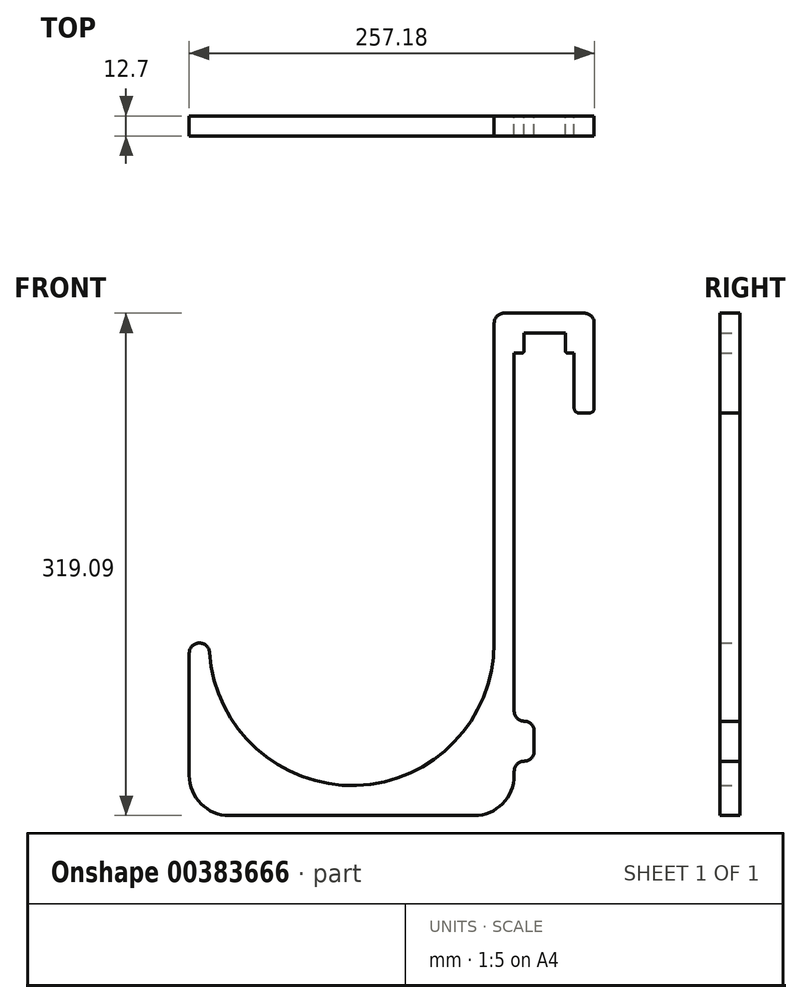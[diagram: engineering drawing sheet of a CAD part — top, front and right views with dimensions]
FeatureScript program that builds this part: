
annotation { "Feature Type Name" : "Feature", "Feature Type Description" : "" }
export const myFeature = defineFeature(function(context is Context, id is Id, definition is map)
    precondition{}
    {
        {
            var Q0;
            Q0=qCreatedBy(makeId("Front.planeOp"),FACE);
            var sketch = newSketch(context, id + "F0", { "sketchPlane" : qUnion([Q0])});
            skArc(sketch, "E0", {"start": v(-90.3, -5.93) * mm, "mid": v(2.97, -90.44) * mm, "end": v(90.49, 0) * mm});
            skLineSegment(sketch, "E1", {"start": v(90.49, 0) * mm, "end": v(90.49, 203.2) * mm});
            skLineSegment(sketch, "E2", {"start": v(96.84, 209.55) * mm, "end": v(147.64, 209.55) * mm});
            skLineSegment(sketch, "E3", {"start": v(153.99, 203.2) * mm, "end": v(153.99, 149.23) * mm});
            skLineSegment(sketch, "E4", {"start": v(150.81, 146.05) * mm, "end": v(144.46, 146.05) * mm});
            skLineSegment(sketch, "E5", {"start": v(141.29, 149.23) * mm, "end": v(141.29, 184.15) * mm});
            skLineSegment(sketch, "E6", {"start": v(103.19, 184.15) * mm, "end": v(103.19, -43.3) * mm});
            skLineSegment(sketch, "E7", {"start": v(109.54, -49.65) * mm, "end": v(109.54, -49.65) * mm});
            skLineSegment(sketch, "E8", {"start": v(115.89, -56) * mm, "end": v(115.89, -68.7) * mm});
            skLineSegment(sketch, "E9", {"start": v(109.54, -75.05) * mm, "end": v(109.54, -75.05) * mm});
            skLineSegment(sketch, "E10", {"start": v(103.19, -81.4) * mm, "end": v(103.19, -84.14) * mm});
            skLineSegment(sketch, "E11", {"start": v(77.79, -109.54) * mm, "end": v(-77.79, -109.54) * mm});
            skLineSegment(sketch, "E12", {"start": v(-103.19, -84.14) * mm, "end": v(-103.19, -6.35) * mm});
            skLineSegment(sketch, "E13", {"start": v(-96.84, 0) * mm, "end": v(-96.63, 0) * mm});
            skPoint(sketch, "E14.visualSharp", {"position": v(90.49, 209.55) * mm});
            skArc(sketch, "E14.filletArc", {"start": v(96.84, 209.55) * mm, "mid": v(92.35, 207.7) * mm, "end": v(90.49, 203.2) * mm});
            skPoint(sketch, "E15.visualSharp", {"position": v(153.99, 209.55) * mm});
            skArc(sketch, "E15.filletArc", {"start": v(153.99, 203.2) * mm, "mid": v(152.13, 207.7) * mm, "end": v(147.64, 209.55) * mm});
            skPoint(sketch, "E16.visualSharp", {"position": v(141.29, 146.05) * mm});
            skArc(sketch, "E16.filletArc", {"start": v(141.29, 149.23) * mm, "mid": v(142.22, 146.98) * mm, "end": v(144.46, 146.05) * mm});
            skPoint(sketch, "E17.visualSharp", {"position": v(153.99, 146.05) * mm});
            skArc(sketch, "E17.filletArc", {"start": v(150.81, 146.05) * mm, "mid": v(153.06, 146.98) * mm, "end": v(153.99, 149.23) * mm});
            skPoint(sketch, "E18.visualSharp", {"position": v(115.89, -49.65) * mm});
            skArc(sketch, "E18.filletArc", {"start": v(115.89, -56) * mm, "mid": v(114.03, -51.5) * mm, "end": v(109.54, -49.65) * mm});
            skPoint(sketch, "E19.visualSharp", {"position": v(115.89, -75.05) * mm});
            skArc(sketch, "E19.filletArc", {"start": v(109.54, -75.05) * mm, "mid": v(114.03, -73.19) * mm, "end": v(115.89, -68.7) * mm});
            skPoint(sketch, "E20.visualSharp", {"position": v(-90.49, 0) * mm});
            skArc(sketch, "E20.filletArc", {"start": v(-90.3, -5.93) * mm, "mid": v(-92.29, -1.71) * mm, "end": v(-96.63, 0) * mm});
            skPoint(sketch, "E21.visualSharp", {"position": v(-103.19, 0) * mm});
            skArc(sketch, "E21.filletArc", {"start": v(-96.84, 0) * mm, "mid": v(-101.33, -1.86) * mm, "end": v(-103.19, -6.35) * mm});
            skPoint(sketch, "E22.visualSharp", {"position": v(-103.19, -109.54) * mm});
            skArc(sketch, "E22.filletArc", {"start": v(-103.19, -84.14) * mm, "mid": v(-95.75, -102.1) * mm, "end": v(-77.79, -109.54) * mm});
            skPoint(sketch, "E23.visualSharp", {"position": v(103.19, -109.54) * mm});
            skArc(sketch, "E23.filletArc", {"start": v(77.79, -109.54) * mm, "mid": v(95.75, -102.1) * mm, "end": v(103.19, -84.14) * mm});
            skLineSegment(sketch, "E24", {"start": v(103.19, 184.15) * mm, "end": v(108.01, 184.15) * mm});
            skLineSegment(sketch, "E25", {"start": v(109.54, 185.67) * mm, "end": v(109.54, 196.85) * mm});
            skLineSegment(sketch, "E26", {"start": v(109.54, 196.85) * mm, "end": v(135.7, 196.85) * mm});
            skLineSegment(sketch, "E27", {"start": v(135.7, 196.85) * mm, "end": v(135.7, 185.67) * mm});
            skLineSegment(sketch, "E28", {"start": v(137.22, 184.15) * mm, "end": v(141.29, 184.15) * mm});
            skPoint(sketch, "E29.visualSharp", {"position": v(109.54, 184.15) * mm});
            skArc(sketch, "E29.filletArc", {"start": v(108.01, 184.15) * mm, "mid": v(109.1, 184.6) * mm, "end": v(109.54, 185.67) * mm});
            skPoint(sketch, "E30.visualSharp", {"position": v(135.7, 184.15) * mm});
            skArc(sketch, "E30.filletArc", {"start": v(135.7, 185.67) * mm, "mid": v(136.15, 184.6) * mm, "end": v(137.22, 184.15) * mm});
            skPoint(sketch, "E31.visualSharp", {"position": v(103.19, -49.65) * mm});
            skArc(sketch, "E31.filletArc", {"start": v(103.19, -43.3) * mm, "mid": v(105.05, -47.79) * mm, "end": v(109.54, -49.65) * mm});
            skPoint(sketch, "E32.visualSharp", {"position": v(103.19, -75.05) * mm});
            skArc(sketch, "E32.filletArc", {"start": v(109.54, -75.05) * mm, "mid": v(105.05, -76.9) * mm, "end": v(103.19, -81.4) * mm});
            skSolve(sketch);
        }
        {
            var Q0;
            Q0=makeQuery(id+"F0.imprint","IMPRINT",FACE,{"disambiguationData":[TD([[makeQuery(id+"F0.imprint","IMPRINT",EDGE,{"derivedFrom":sQuery(id+"F0.wireOp",EDGE,"E0")}),-1.0]])]});
            extrude(context, id + "F1", {"entities" : qUnion([Q0]), "depth" : 12.7 * mm});
        }
    });
